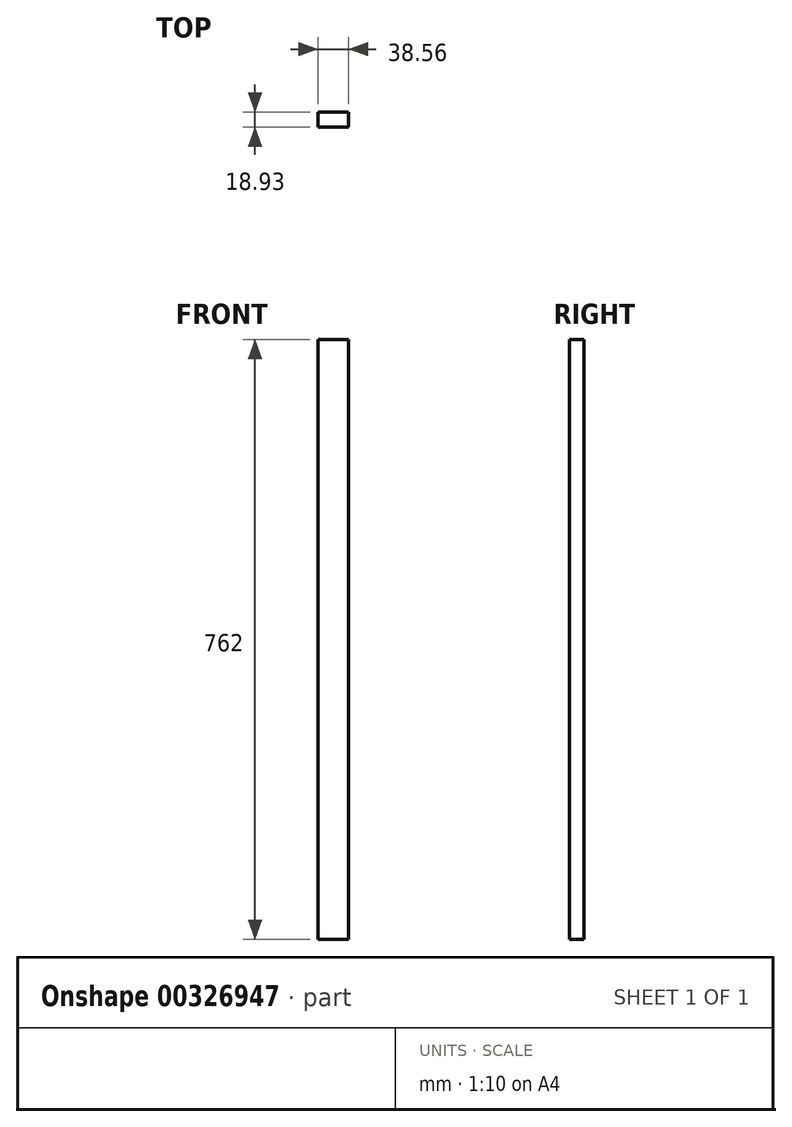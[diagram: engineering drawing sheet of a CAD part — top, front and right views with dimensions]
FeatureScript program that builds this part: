
annotation { "Feature Type Name" : "Feature", "Feature Type Description" : "" }
export const myFeature = defineFeature(function(context is Context, id is Id, definition is map)
    precondition{}
    {
        {
            var Q0;
            Q0=qCreatedBy(makeId("Top.planeOp"),FACE);
            var sketch = newSketch(context, id + "F0", { "sketchPlane" : qUnion([Q0])});
            skLineSegment(sketch, "E0.bottom", {"start": v(-139.25, -78.55) * mm, "end": v(-100.7, -78.55) * mm});
            skLineSegment(sketch, "E0.top", {"start": v(-139.25, -97.48) * mm, "end": v(-100.7, -97.48) * mm});
            skLineSegment(sketch, "E0.left", {"start": v(-139.25, -78.55) * mm, "end": v(-139.25, -97.48) * mm});
            skLineSegment(sketch, "E0.right", {"start": v(-100.7, -78.55) * mm, "end": v(-100.7, -97.48) * mm});
            skSolve(sketch);
        }
        {
            var Q0;
            Q0 = qSketchRegion(id + "F0", true);
            extrude(context, id + "F1", {"entities" : qUnion([Q0]), "depth" : 762 * mm});
        }
    });
